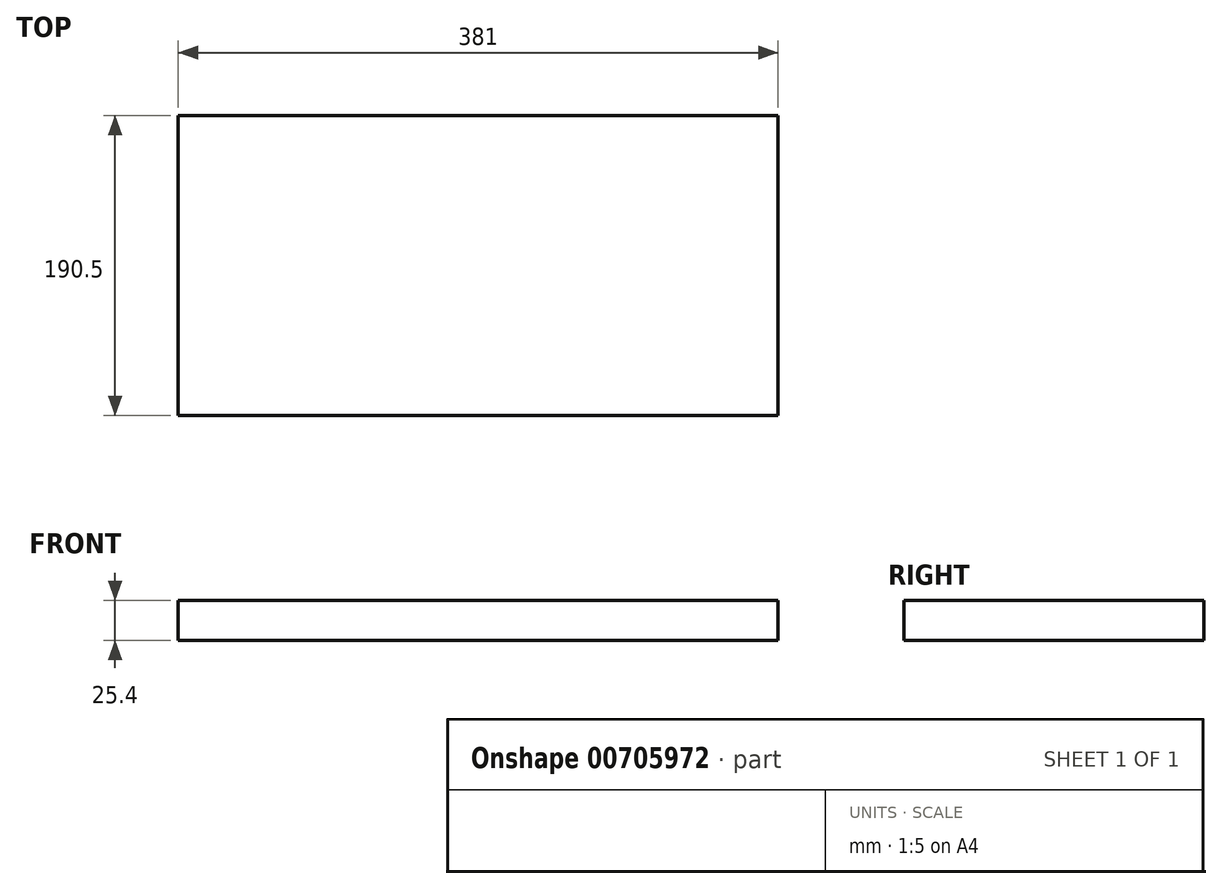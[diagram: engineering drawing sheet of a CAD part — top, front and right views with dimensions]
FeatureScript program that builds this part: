
annotation { "Feature Type Name" : "Feature", "Feature Type Description" : "" }
export const myFeature = defineFeature(function(context is Context, id is Id, definition is map)
    precondition{}
    {
        {
            var Q0;
            Q0=qCreatedBy(makeId("Top.planeOp"),FACE);
            var sketch = newSketch(context, id + "F0", { "sketchPlane" : qUnion([Q0])});
            skLineSegment(sketch, "E0.bottom", {"start": v(-203.66, 70.11) * mm, "end": v(177.34, 70.11) * mm});
            skLineSegment(sketch, "E0.top", {"start": v(-203.66, -120.39) * mm, "end": v(177.34, -120.39) * mm});
            skLineSegment(sketch, "E0.left", {"start": v(-203.66, 70.11) * mm, "end": v(-203.66, -120.39) * mm});
            skLineSegment(sketch, "E0.right", {"start": v(177.34, 70.11) * mm, "end": v(177.34, -120.39) * mm});
            skSolve(sketch);
        }
        {
            var Q0;
            Q0=makeQuery(id+"F0.imprint","IMPRINT",FACE,{"disambiguationData":[TD([[makeQuery(id+"F0.imprint","IMPRINT",EDGE,{"derivedFrom":sQuery(id+"F0.wireOp",EDGE,"E0.bottom")}),-1.0]])]});
            extrude(context, id + "F1", {"entities" : qUnion([Q0]), "depth" : 25.4 * mm, "offsetDistance" : 25.4 * mm});
        }
    });
